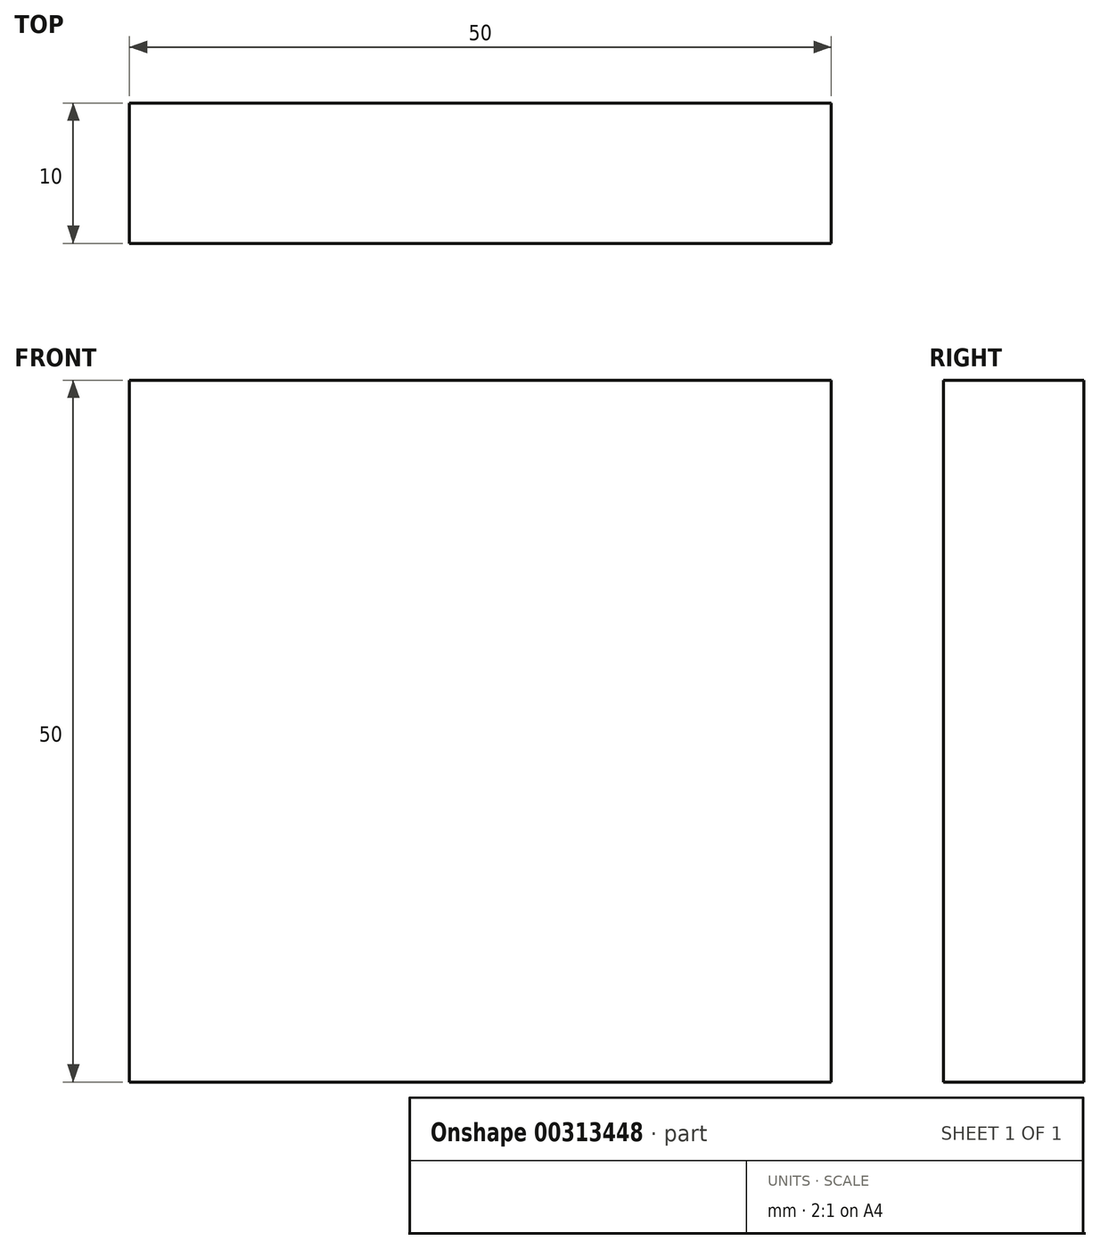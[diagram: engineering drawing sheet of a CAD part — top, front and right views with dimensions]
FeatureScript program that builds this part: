
annotation { "Feature Type Name" : "Feature", "Feature Type Description" : "" }
export const myFeature = defineFeature(function(context is Context, id is Id, definition is map)
    precondition{}
    {
        {
            var Q0;
            Q0=qCreatedBy(makeId("Front.planeOp"),FACE);
            var sketch = newSketch(context, id + "F0", { "sketchPlane" : qUnion([Q0])});
            skLineSegment(sketch, "E0.bottom", {"start": v(25, 25) * mm, "end": v(-25, 25) * mm});
            skLineSegment(sketch, "E0.top", {"start": v(25, -25) * mm, "end": v(-25, -25) * mm});
            skLineSegment(sketch, "E0.left", {"start": v(25, 25) * mm, "end": v(25, -25) * mm});
            skLineSegment(sketch, "E0.right", {"start": v(-25, 25) * mm, "end": v(-25, -25) * mm});
            skPoint(sketch, "E0.middle", {"position": v(0, 0) * mm});
            skSolve(sketch);
        }
        {
            var Q0;
            Q0=makeQuery(id+"F0.imprint","IMPRINT",FACE,{"disambiguationData":[TD([[makeQuery(id+"F0.imprint","IMPRINT",EDGE,{"derivedFrom":sQuery(id+"F0.wireOp",EDGE,"E0.bottom")}),1.0]])]});
            extrude(context, id + "F1", {"entities" : qUnion([Q0]), "depth" : 10 * mm});
        }
    });
